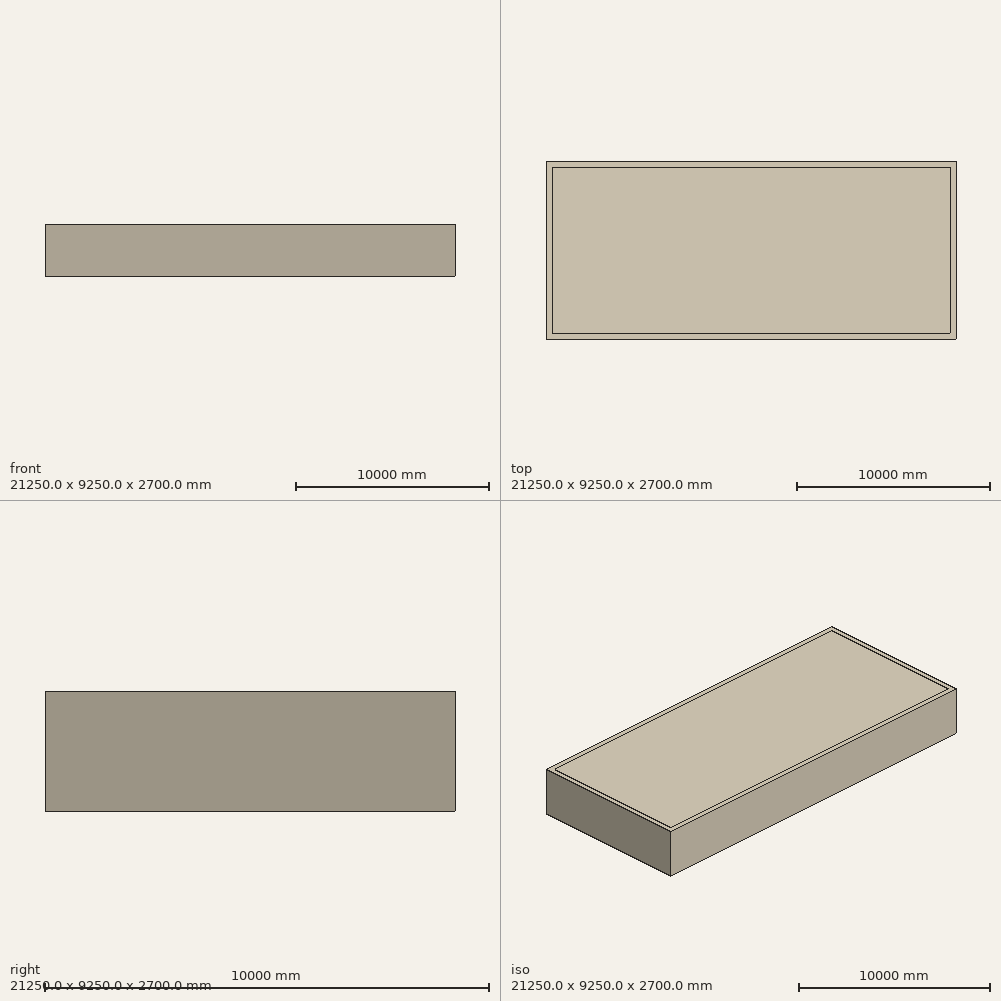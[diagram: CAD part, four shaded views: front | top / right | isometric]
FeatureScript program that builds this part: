
annotation { "Feature Type Name" : "Feature", "Feature Type Description" : "" }
export const myFeature = defineFeature(function(context is Context, id is Id, definition is map)
    precondition{}
    {
        {
            var Q0;
            Q0=qCreatedBy(makeId("Top.planeOp"),FACE);
            var sketch = newSketch(context, id + "F0", { "sketchPlane" : qUnion([Q0])});
            skLineSegment(sketch, "E0.bottom", {"start": v(0, 0) * mm, "end": v(21250, 0) * mm});
            skLineSegment(sketch, "E0.top", {"start": v(0, -9250) * mm, "end": v(21250, -9250) * mm});
            skLineSegment(sketch, "E0.left", {"start": v(0, 0) * mm, "end": v(0, -9250) * mm});
            skLineSegment(sketch, "E0.right", {"start": v(21250, 0) * mm, "end": v(21250, -9250) * mm});
            skSolve(sketch);
        }
        {
            var Q0;
            Q0=qSketchRegion(id+"F0",true);
            extrude(context, id + "F1", {"entities" : qUnion([Q0]), "depth" : 150 * mm, "offsetDistance" : 25 * mm});
        }
        {
            var Q0;
            Q0=makeQuery(id+"F1.opExtrude","CAP_FACE",FACE,{"disambiguationData":[OSD([sQuery(id+"F0.wireOp",EDGE,"E0.bottom"),sQuery(id+"F0.wireOp",EDGE,"E0.top"),sQuery(id+"F0.wireOp",EDGE,"E0.left"),sQuery(id+"F0.wireOp",EDGE,"E0.right")])],"isStart":false});
            var sketch = newSketch(context, id + "F2", { "sketchPlane" : qUnion([Q0])});
            skLineSegment(sketch, "E1.0.0", {"start": v(0, 0) * mm, "end": v(0, -9250) * mm});
            skLineSegment(sketch, "E1.0.1", {"start": v(0, -9250) * mm, "end": v(21250, -9250) * mm});
            skLineSegment(sketch, "E1.0.2", {"start": v(21250, -9250) * mm, "end": v(21250, 0) * mm});
            skLineSegment(sketch, "E1.0.3", {"start": v(21250, 0) * mm, "end": v(0, 0) * mm});
            skLineSegment(sketch, "E2.0", {"start": v(300, -300) * mm, "end": v(300, -8950) * mm});
            skLineSegment(sketch, "E2.1", {"start": v(20950, -300) * mm, "end": v(300, -300) * mm});
            skLineSegment(sketch, "E2.2", {"start": v(20950, -8950) * mm, "end": v(20950, -300) * mm});
            skLineSegment(sketch, "E2.3", {"start": v(300, -8950) * mm, "end": v(20950, -8950) * mm});
            skSolve(sketch);
        }
        {
            var Q0;
            Q0=qSketchRegion(id+"F2",true);
            extrude(context, id + "F3", {"entities" : qUnion([Q0]), "operationType" : NewBodyOperationType.ADD, "depth" : 2550 * mm, "offsetDistance" : 25 * mm});
        }
        {
            var Q0;
            Q0=makeQuery(id+"F1.opExtrude","CAP_FACE",FACE,{"disambiguationData":[OSD([sQuery(id+"F0.wireOp",EDGE,"E0.bottom"),sQuery(id+"F0.wireOp",EDGE,"E0.top"),sQuery(id+"F0.wireOp",EDGE,"E0.left"),sQuery(id+"F0.wireOp",EDGE,"E0.right")])],"isStart":false});
            var Q1;
            Q1=makeQuery(id+"F3.opExtrude","CAP_VERTEX",VERTEX,{"disambiguationData":[OSD([sQuery(id+"F2.wireOp",EDGE,"E1.0.0"),sQuery(id+"F2.wireOp",EDGE,"E1.0.3")])],"isStart":false});
            extrude(context, id + "F4", {"entities" : qUnion([Q0]), "endBound" : BoundingType.UP_TO_VERTEX, "depth" : 25 * mm, "endBoundEntityVertex" : qUnion([Q1]), "offsetDistance" : 25 * mm});
        }
    });
